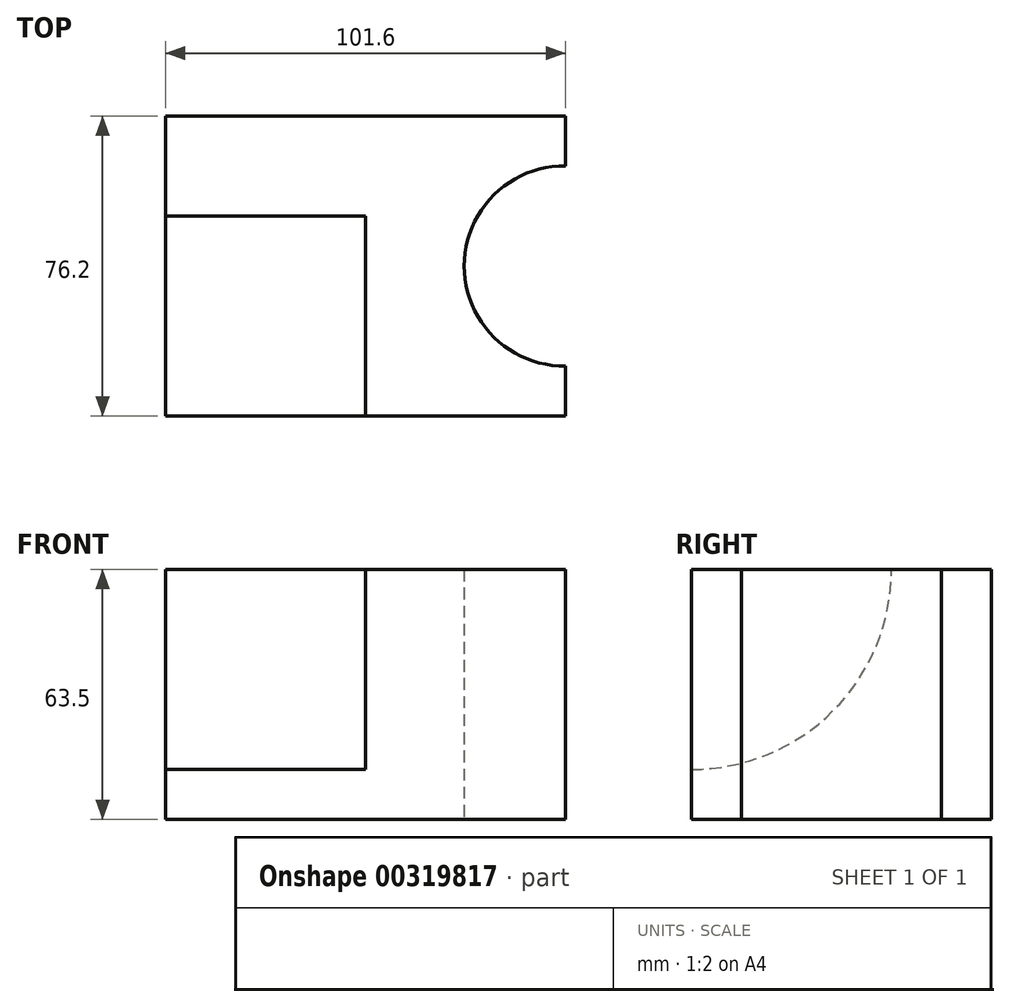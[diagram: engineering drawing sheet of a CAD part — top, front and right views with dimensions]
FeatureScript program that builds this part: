
annotation { "Feature Type Name" : "Feature", "Feature Type Description" : "" }
export const myFeature = defineFeature(function(context is Context, id is Id, definition is map)
    precondition{}
    {
        {
            var Q0;
            Q0=qCreatedBy(makeId("Top.planeOp"),FACE);
            var sketch = newSketch(context, id + "F0", { "sketchPlane" : qUnion([Q0])});
            skLineSegment(sketch, "E0.bottom", {"start": v(-48.81, 43.03) * mm, "end": v(52.79, 43.03) * mm});
            skLineSegment(sketch, "E0.top", {"start": v(-48.81, -33.17) * mm, "end": v(52.79, -33.17) * mm});
            skLineSegment(sketch, "E0.left", {"start": v(-48.81, 43.03) * mm, "end": v(-48.81, -33.17) * mm});
            skLineSegment(sketch, "E0.right", {"start": v(52.79, 43.03) * mm, "end": v(52.79, -33.17) * mm});
            skArc(sketch, "E1", {"start": v(52.79, 30.33) * mm, "mid": v(27.04, 4.93) * mm, "end": v(52.79, -20.47) * mm});
            skSolve(sketch);
        }
        {
            var Q0;
            {var subQ1=sQuery(id+"F0.wireOp",EDGE,"E0.bottom");Q0=makeQuery(id+"F0.imprint","IMPRINT",FACE,{"disambiguationData":[TD([[makeQuery(id+"F0.imprint","IMPRINT",EDGE,{"derivedFrom":subQ1}),-1.0]])]});}
            extrude(context, id + "F1", {"entities" : qUnion([Q0]), "depth" : 63.5 * mm});
        }
        {
            var Q0;
            Q0=makeQuery(id+"F1.opExtrude","SWEPT_FACE",FACE,{"disambiguationData":[OSD([sQuery(id+"F0.wireOp",EDGE,"E0.left")])]});
            var sketch = newSketch(context, id + "F2", { "sketchPlane" : qUnion([Q0])});
            skLineSegment(sketch, "E2", {"start": v(-43.03, 63.5) * mm, "end": v(-17.63, 63.5) * mm});
            skLineSegment(sketch, "E3", {"start": v(33.17, 0) * mm, "end": v(33.17, 12.7) * mm});
            skArc(sketch, "E4", {"start": v(-17.63, 63.5) * mm, "mid": v(-2.76, 27.57) * mm, "end": v(33.17, 12.7) * mm});
            skSolve(sketch);
        }
        {
            var Q0;
            {var subQ0=sQuery(id+"F2.wireOp",EDGE,"E4");Q0=makeQuery(id+"F2.imprint","IMPRINT",FACE,{"disambiguationData":[TD([[makeQuery(id+"F2.imprint","IMPRINT",EDGE,{"derivedFrom":subQ0}),1.0]])]});}
            extrude(context, id + "F3", {"entities" : qUnion([Q0]), "operationType" : NewBodyOperationType.REMOVE, "oppositeDirection" : true, "depth" : 50.8 * mm});
        }
    });
